# Revit family: Shower_Elbow-GROHE-Relexa-28627_Series
name_source: partatom
category: Plumbing Fixtures
revit_build: Autodesk Revit 2014 (Build: 20130308_1515(x64)
units: mm (PartAtom-declared; Revit-internal decimal feet)

## types (2) — shared parameters
ADA Compliant = Yes
Assembly Code = D2020
CW Connection = Yes
CWFU = 2
Connection Diameter = 1/2"
Default Elevation = 68"
Description = Relexa Shower Outlet Elbow
HW Connection = Yes
HWFU = 3
Height = 2 5/8"
Installation Type = Wall Mounted
Length = 2 1/2"
Manufacturer = GROHE
Price = Prices may vary. Please consult Manufacturer Representative for most up-to-date price list.
Product Page URL = http://www.grohe.com
Shipping Weight = 0.344 lb
URL = http://www.grohe.com
Vent Connection = No
WFU = 4
Warranty Information = Limited Lifetime Warranty
Waste Connection = No
Width = 2 5/8"

## per-type parameters (varying)
| type | Finish | Material |
| 28627000 | Brass-Grohe-000-Starlight Chrome | Brass-Grohe-000-Starlight Chrome |
| 28627EN0 | Brass-Grohe-EN0-Brushed Nickel | Brass-Grohe-EN0-Brushed Nickel |

note: column(s) folded — value = type name in every type: Model

## geometry (parser evidence)
native form markers: Sweep x3
no freeform markers — native parametric forms only
